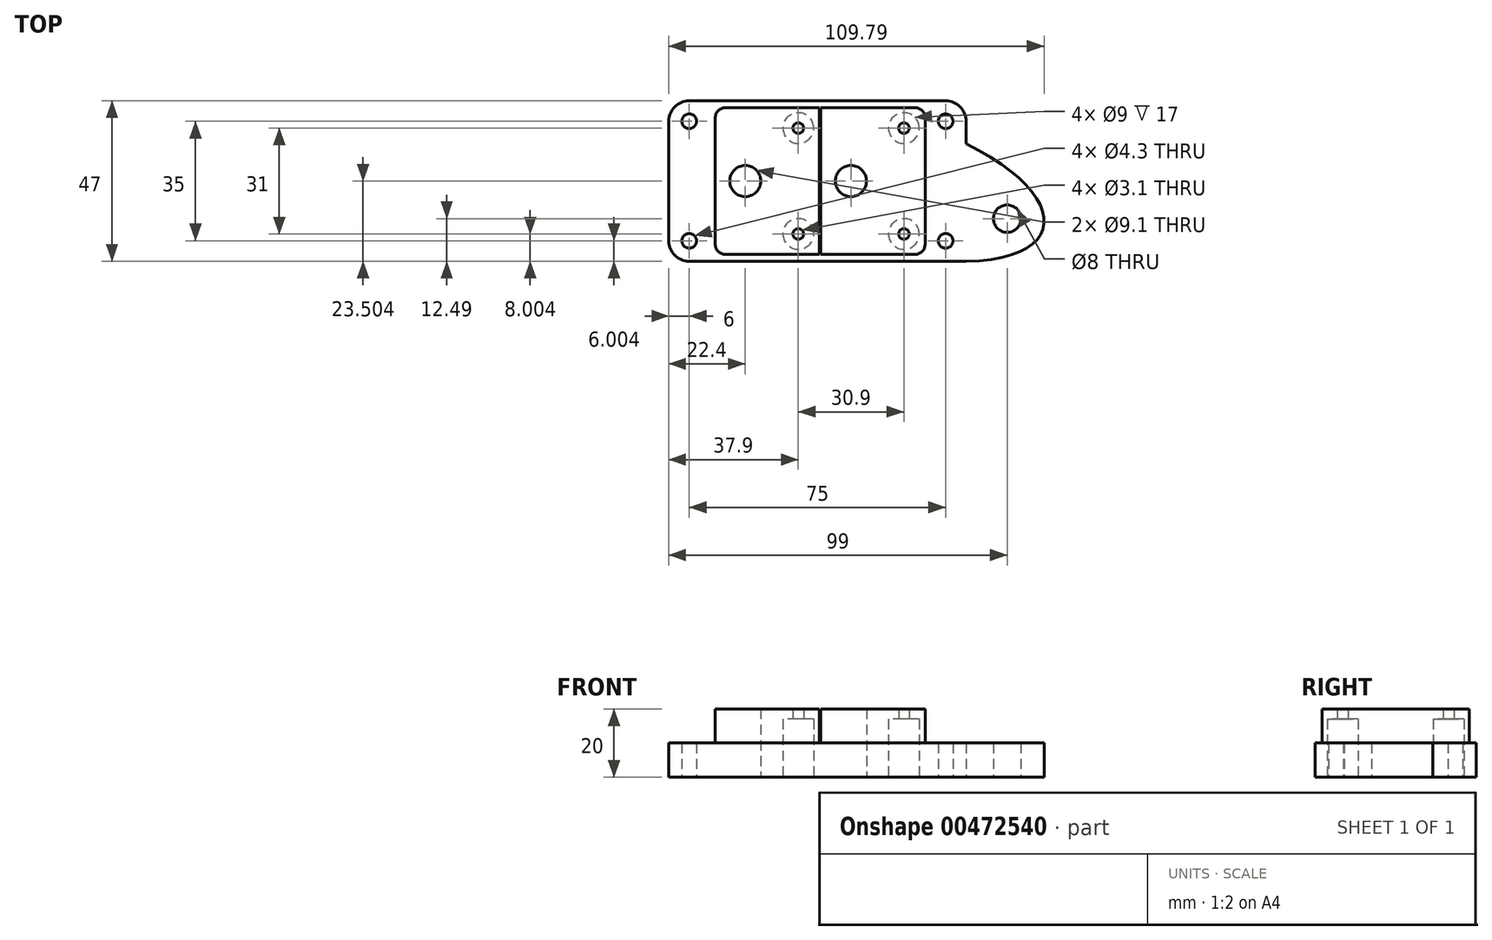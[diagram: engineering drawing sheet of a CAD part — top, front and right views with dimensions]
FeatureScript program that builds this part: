
annotation { "Feature Type Name" : "Feature", "Feature Type Description" : "" }
export const myFeature = defineFeature(function(context is Context, id is Id, definition is map)
    precondition{}
    {
        {
            var Q0;
            Q0=qCreatedBy(makeId("Top.planeOp"),FACE);
            var sketch = newSketch(context, id + "F0", { "sketchPlane" : qUnion([Q0])});
            skCircle(sketch, "E0", {"center": v(39.69, 25.97) * mm, "radius": 4.55 * mm});
            skLineSegment(sketch, "E1", {"start": v(55.19, 43.37) * mm, "end": v(55.19, 7.74) * mm, "construction": true});
            skLineSegment(sketch, "E2", {"start": v(56.48, 41.47) * mm, "end": v(36.33, 41.47) * mm, "construction": true});
            skLineSegment(sketch, "E3", {"start": v(57.08, 10.47) * mm, "end": v(36.49, 10.47) * mm, "construction": true});
            skCircle(sketch, "E4", {"center": v(55.19, 41.47) * mm, "radius": 1.55 * mm});
            skCircle(sketch, "E5", {"center": v(55.19, 10.47) * mm, "radius": 1.55 * mm});
            skLineSegment(sketch, "E6.bottom", {"start": v(30.89, 47.47) * mm, "end": v(61.39, 47.47) * mm});
            skLineSegment(sketch, "E6.top", {"start": v(30.89, 4.47) * mm, "end": v(61.39, 4.47) * mm});
            skLineSegment(sketch, "E6.left", {"start": v(30.89, 47.47) * mm, "end": v(30.89, 4.47) * mm});
            skLineSegment(sketch, "E6.right", {"start": v(61.39, 47.47) * mm, "end": v(61.39, 4.47) * mm});
            skLineSegment(sketch, "E7.bottom", {"start": v(41.82, 4.47) * mm, "end": v(53.52, 4.47) * mm});
            skCircle(sketch, "E8", {"center": v(55.19, 10.47) * mm, "radius": 4.5 * mm});
            skCircle(sketch, "E9", {"center": v(55.19, 41.47) * mm, "radius": 4.5 * mm});
            skLineSegment(sketch, "E10.bottom", {"start": v(-13.61, 49.47) * mm, "end": v(73.39, 49.47) * mm});
            skLineSegment(sketch, "E10.top", {"start": v(-13.61, 2.47) * mm, "end": v(73.39, 2.47) * mm});
            skLineSegment(sketch, "E10.left", {"start": v(-13.61, 49.47) * mm, "end": v(-13.61, 2.47) * mm});
            skLineSegment(sketch, "E10.right", {"start": v(73.39, 49.47) * mm, "end": v(73.39, 2.47) * mm});
            skCircle(sketch, "E11", {"center": v(8.79, 25.97) * mm, "radius": 4.55 * mm});
            skLineSegment(sketch, "E12", {"start": v(24.29, 43.37) * mm, "end": v(24.29, 7.74) * mm, "construction": true});
            skLineSegment(sketch, "E13", {"start": v(25.58, 41.47) * mm, "end": v(5.43, 41.47) * mm, "construction": true});
            skLineSegment(sketch, "E14", {"start": v(26.18, 10.47) * mm, "end": v(5.59, 10.47) * mm, "construction": true});
            skCircle(sketch, "E15", {"center": v(24.29, 41.47) * mm, "radius": 1.55 * mm});
            skCircle(sketch, "E16", {"center": v(24.29, 10.47) * mm, "radius": 1.55 * mm});
            skLineSegment(sketch, "E17.bottom", {"start": v(-0.01, 47.47) * mm, "end": v(30.49, 47.47) * mm});
            skLineSegment(sketch, "E17.top", {"start": v(-0.01, 4.47) * mm, "end": v(30.49, 4.47) * mm});
            skLineSegment(sketch, "E17.left", {"start": v(-0.01, 47.47) * mm, "end": v(-0.01, 4.47) * mm});
            skLineSegment(sketch, "E17.right", {"start": v(30.49, 47.47) * mm, "end": v(30.49, 4.47) * mm});
            skLineSegment(sketch, "E18.bottom", {"start": v(8.92, 4.47) * mm, "end": v(20.62, 4.47) * mm});
            skCircle(sketch, "E19", {"center": v(24.29, 10.47) * mm, "radius": 4.5 * mm});
            skCircle(sketch, "E20", {"center": v(24.29, 41.47) * mm, "radius": 4.5 * mm});
            skCircle(sketch, "E21", {"center": v(-7.61, 43.47) * mm, "radius": 2.15 * mm});
            skCircle(sketch, "E22", {"center": v(-7.61, 8.47) * mm, "radius": 2.15 * mm});
            skCircle(sketch, "E23", {"center": v(67.39, 43.47) * mm, "radius": 2.15 * mm});
            skCircle(sketch, "E24", {"center": v(67.39, 8.47) * mm, "radius": 2.15 * mm});
            skCircle(sketch, "E25", {"center": v(85.39, 14.96) * mm, "radius": 4 * mm});
            skFitSpline(sketch, "E26", {"points": [v(73.39, 2.47) * mm, v(73.39, 36.84) * mm], "startDerivative": vector(92.37, 1.47) * mm, "endDerivative": vector(-89.95, 43.55) * mm});
            skSolve(sketch);
        }
        {
            var Q0;
            Q0=makeQuery(id+"F0.imprint","IMPRINT",FACE,{"disambiguationData":[TD([[makeQuery(id+"F0.imprint","IMPRINT",EDGE,{"derivedFrom":sQuery(id+"F0.wireOp",EDGE,"E6.bottom")}),1.0]])]});
            var Q1;
            Q1=makeQuery(id+"F0.imprint","IMPRINT",FACE,{"disambiguationData":[TD([[makeQuery(id+"F0.imprint","IMPRINT",EDGE,{"derivedFrom":sQuery(id+"F0.wireOp",EDGE,"E25")}),-1.0]])]});
            extrude(context, id + "F1", {"entities" : qUnion([Q0, Q1]), "depth" : 10 * mm, "offsetDistance" : 25 * mm});
        }
        {
            var Q0;
            Q0=makeQuery(id+"F0.imprint","IMPRINT",FACE,{"disambiguationData":[TD([[makeQuery(id+"F0.imprint","IMPRINT",EDGE,{"derivedFrom":sQuery(id+"F0.wireOp",EDGE,"E11")}),-1.0]])]});
            var Q1;
            Q1=makeQuery(id+"F0.imprint","IMPRINT",FACE,{"disambiguationData":[TD([[makeQuery(id+"F0.imprint","IMPRINT",EDGE,{"derivedFrom":sQuery(id+"F0.wireOp",EDGE,"E0")}),-1.0]])]});
            extrude(context, id + "F2", {"entities" : qUnion([Q0, Q1]), "operationType" : NewBodyOperationType.ADD, "depth" : 20 * mm, "offsetDistance" : 25 * mm});
        }
        {
            var Q0;
            Q0=makeQuery(id+"F0.imprint","IMPRINT",FACE,{"disambiguationData":[TD([[makeQuery(id+"F0.imprint","IMPRINT",EDGE,{"derivedFrom":sQuery(id+"F0.wireOp",EDGE,"E15")}),-1.0]])]});
            var Q1;
            Q1=makeQuery(id+"F0.imprint","IMPRINT",FACE,{"disambiguationData":[TD([[makeQuery(id+"F0.imprint","IMPRINT",EDGE,{"derivedFrom":sQuery(id+"F0.wireOp",EDGE,"E4")}),-1.0]])]});
            var Q2;
            Q2=makeQuery(id+"F0.imprint","IMPRINT",FACE,{"disambiguationData":[TD([[makeQuery(id+"F0.imprint","IMPRINT",EDGE,{"derivedFrom":sQuery(id+"F0.wireOp",EDGE,"E5")}),-1.0]])]});
            var Q3;
            Q3=makeQuery(id+"F0.imprint","IMPRINT",FACE,{"disambiguationData":[TD([[makeQuery(id+"F0.imprint","IMPRINT",EDGE,{"derivedFrom":sQuery(id+"F0.wireOp",EDGE,"E16")}),-1.0]])]});
            extrude(context, id + "F3", {"entities" : qUnion([Q0, Q1, Q2, Q3]), "operationType" : NewBodyOperationType.ADD, "depth" : 20 * mm, "offsetDistance" : 25 * mm, "hasSecondDirection" : true, "secondDirectionOppositeDirection" : true, "secondDirectionDepth" : -17 * mm});
        }
        {
            var Q0;
            Q0=makeQuery(id+"F1.opExtrude","SWEPT_EDGE",EDGE,{"disambiguationData":[OSD([sQuery(id+"F0.wireOp",EDGE,"E10.top"),sQuery(id+"F0.wireOp",EDGE,"E10.right")])]});
            var Q1;
            Q1=makeQuery(id+"F1.opExtrude","SWEPT_EDGE",EDGE,{"disambiguationData":[OSD([sQuery(id+"F0.wireOp",EDGE,"E10.bottom"),sQuery(id+"F0.wireOp",EDGE,"E10.right")])]});
            var Q2;
            Q2=makeQuery(id+"F1.opExtrude","SWEPT_EDGE",EDGE,{"disambiguationData":[OSD([sQuery(id+"F0.wireOp",EDGE,"E10.bottom"),sQuery(id+"F0.wireOp",EDGE,"E10.left")])]});
            var Q3;
            Q3=makeQuery(id+"F1.opExtrude","SWEPT_EDGE",EDGE,{"disambiguationData":[OSD([sQuery(id+"F0.wireOp",EDGE,"E10.top"),sQuery(id+"F0.wireOp",EDGE,"E10.left")])]});
            fillet(context, id + "F4", {"entities" : qUnion([Q0, Q1, Q2, Q3]), "radius" : 6 * mm, "tangentPropagation" : true, "allowEdgeOverflow" : false});
        }
        {
            var Q0;
            Q0=makeQuery(id+"F2.opExtrude","SWEPT_EDGE",EDGE,{"disambiguationData":[OSD([sQuery(id+"F0.wireOp",EDGE,"E17.top"),sQuery(id+"F0.wireOp",EDGE,"E17.left")])]});
            var Q1;
            Q1=makeQuery(id+"F2.opExtrude","SWEPT_EDGE",EDGE,{"disambiguationData":[OSD([sQuery(id+"F0.wireOp",EDGE,"E6.top"),sQuery(id+"F0.wireOp",EDGE,"E6.right")])]});
            var Q2;
            Q2=makeQuery(id+"F2.opExtrude","SWEPT_EDGE",EDGE,{"disambiguationData":[OSD([sQuery(id+"F0.wireOp",EDGE,"E6.bottom"),sQuery(id+"F0.wireOp",EDGE,"E6.right")])]});
            var Q3;
            Q3=makeQuery(id+"F2.opExtrude","SWEPT_EDGE",EDGE,{"disambiguationData":[OSD([sQuery(id+"F0.wireOp",EDGE,"E17.bottom"),sQuery(id+"F0.wireOp",EDGE,"E17.left")])]});
            fillet(context, id + "F5", {"entities" : qUnion([Q0, Q1, Q2, Q3]), "radius" : 3 * mm, "tangentPropagation" : true, "allowEdgeOverflow" : false});
        }
    });
